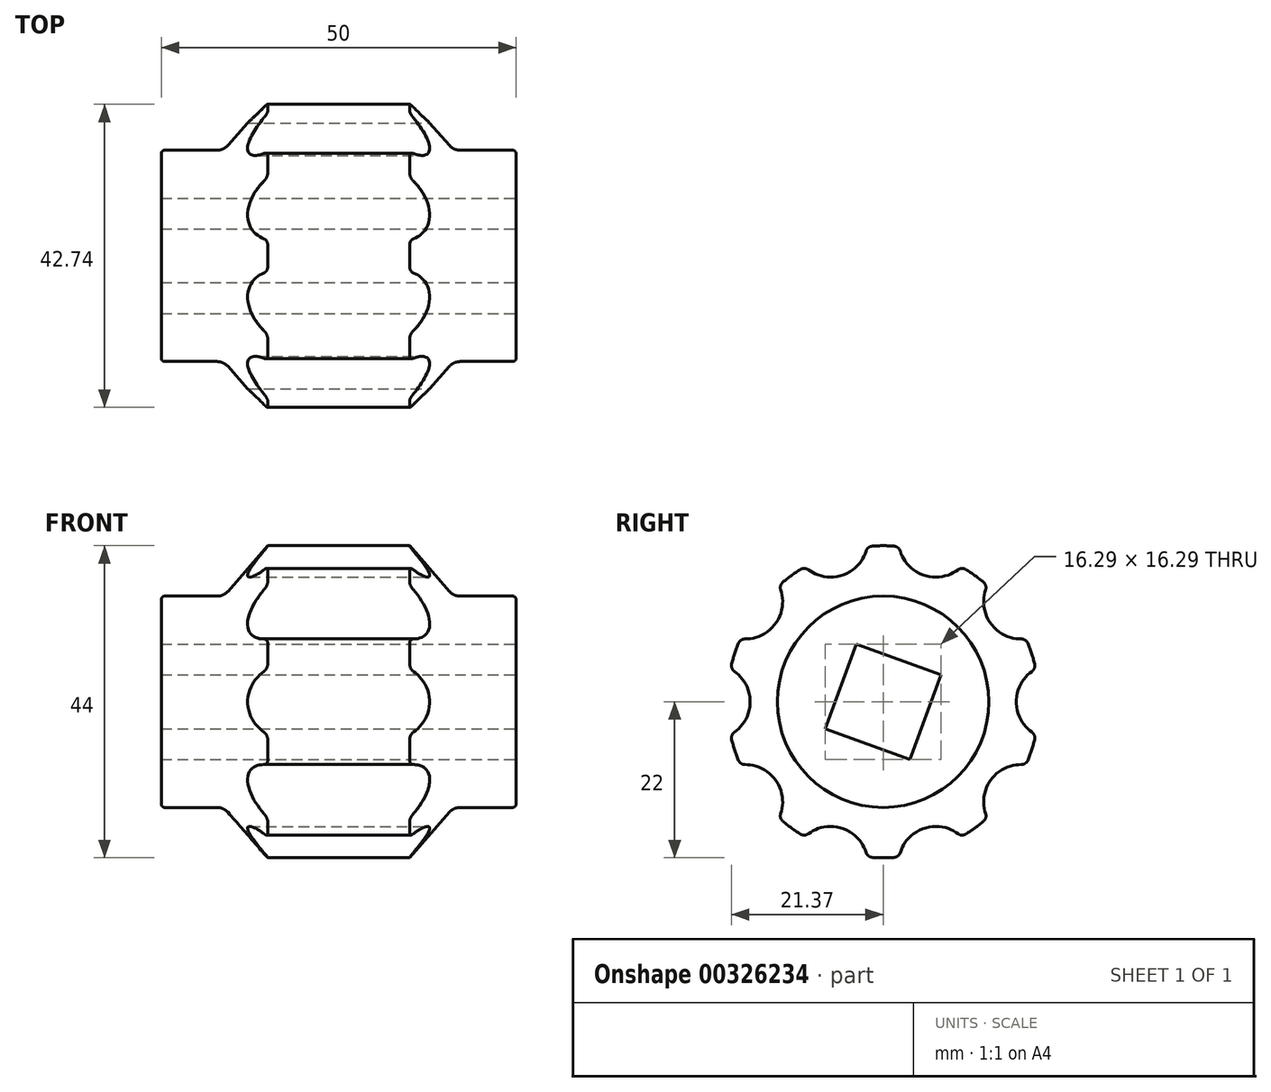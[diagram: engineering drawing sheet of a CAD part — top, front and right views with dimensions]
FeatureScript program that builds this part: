
annotation { "Feature Type Name" : "Feature", "Feature Type Description" : "" }
export const myFeature = defineFeature(function(context is Context, id is Id, definition is map)
    precondition{}
    {
        {
            var Q0;
            Q0=qCreatedBy(makeId("Front.planeOp"),FACE);
            var sketch = newSketch(context, id + "F0", { "sketchPlane" : qUnion([Q0])});
            skLineSegment(sketch, "E0", {"start": v(23, 5) * mm, "end": v(23, 14.9) * mm});
            skLineSegment(sketch, "E1", {"start": v(23, 14.9) * mm, "end": v(14.2, 14.9) * mm});
            skLineSegment(sketch, "E2", {"start": v(8, 22) * mm, "end": v(-12, 22) * mm});
            skLineSegment(sketch, "E3", {"start": v(-27, 14.9) * mm, "end": v(-27, 5) * mm});
            skLineSegment(sketch, "E4", {"start": v(-27, 5) * mm, "end": v(23, 5) * mm});
            skPoint(sketch, "E5.start.orphan", {"position": v(-27, 0) * mm});
            skLineSegment(sketch, "E6", {"start": v(-27, 0) * mm, "end": v(30.22, 0) * mm, "construction": true});
            skLineSegment(sketch, "E7", {"start": v(8, 22) * mm, "end": v(14.2, 14.9) * mm});
            skLineSegment(sketch, "E8", {"start": v(-27, 14.9) * mm, "end": v(-18.2, 14.9) * mm});
            skLineSegment(sketch, "E9", {"start": v(-18.2, 14.9) * mm, "end": v(-12, 22) * mm});
            skSolve(sketch);
        }
        {
            var Q0;
            Q0=makeQuery(id+"F0.imprint","IMPRINT",FACE,{"disambiguationData":[TD([[makeQuery(id+"F0.imprint","IMPRINT",EDGE,{"derivedFrom":sQuery(id+"F0.wireOp",EDGE,"E0")}),1.0]])]});
            var Q1;
            Q1=sQuery(id+"F0.wireOp",EDGE,"E6");
            revolve(context, id + "F1", {"entities" : qUnion([Q0]), "axis" : qUnion([Q1]), "revolveType" : RevolveType.FULL});
        }
        {
            var Q0;
            Q0=makeQuery(id+"F1.opRevolve","SWEPT_FACE",FACE,{"disambiguationData":[OSD([sQuery(id+"F0.wireOp",EDGE,"E0")])]});
            var sketch = newSketch(context, id + "F2", { "sketchPlane" : qUnion([Q0])});
            skCircle(sketch, "E10.cCircle", {"center": v(0, 0) * mm, "radius": 6.35 * mm, "construction": true});
            skLineSegment(sketch, "E10.0", {"start": v(8.14, 3.79) * mm, "end": v(3.79, -8.14) * mm});
            skLineSegment(sketch, "E10.1", {"start": v(3.79, -8.14) * mm, "end": v(-8.14, -3.79) * mm});
            skLineSegment(sketch, "E10.2", {"start": v(-8.14, -3.79) * mm, "end": v(-3.79, 8.14) * mm});
            skLineSegment(sketch, "E10.3", {"start": v(-3.79, 8.14) * mm, "end": v(8.14, 3.79) * mm});
            skPoint(sketch, "E10.0.midPoint", {"position": v(5.96, -2.18) * mm});
            skCircle(sketch, "E11", {"center": v(24, 0) * mm, "radius": 5.25 * mm});
            skCircle(sketch, "E12.1.0", {"center": v(19.42, 14.1) * mm, "radius": 5.25 * mm});
            skCircle(sketch, "E12.2.0", {"center": v(7.42, 22.83) * mm, "radius": 5.25 * mm});
            skCircle(sketch, "E12.3.0", {"center": v(-7.42, 22.83) * mm, "radius": 5.25 * mm});
            skCircle(sketch, "E12.4.0", {"center": v(-19.42, 14.1) * mm, "radius": 5.25 * mm});
            skCircle(sketch, "E12.5.0", {"center": v(-24, 0) * mm, "radius": 5.25 * mm});
            skCircle(sketch, "E12.6.0", {"center": v(-19.42, -14.1) * mm, "radius": 5.25 * mm});
            skCircle(sketch, "E12.7.0", {"center": v(-7.42, -22.83) * mm, "radius": 5.25 * mm});
            skCircle(sketch, "E12.8.0", {"center": v(7.42, -22.83) * mm, "radius": 5.25 * mm});
            skCircle(sketch, "E12.9.0", {"center": v(19.42, -14.1) * mm, "radius": 5.25 * mm});
            skSolve(sketch);
        }
        {
            var Q0;
            Q0=makeQuery(id+"F1.opRevolve","SWEPT_EDGE",EDGE,{"disambiguationData":[OSD([sQuery(id+"F0.wireOp",EDGE,"E3"),sQuery(id+"F0.wireOp",EDGE,"E8")])]});
            var Q1;
            Q1=makeQuery(id+"F1.opRevolve","SWEPT_EDGE",EDGE,{"disambiguationData":[OSD([sQuery(id+"F0.wireOp",EDGE,"E0"),sQuery(id+"F0.wireOp",EDGE,"E1")])]});
            fillet(context, id + "F3", {"entities" : qUnion([Q0, Q1]), "radius" : .5 * mm, "tangentPropagation" : true, "allowEdgeOverflow" : false});
        }
        {
            var Q0;
            Q0=makeQuery(id+"F2.imprint","IMPRINT",FACE,{"disambiguationData":[TD([[makeQuery(id+"F2.imprint","IMPRINT",EDGE,{"derivedFrom":sQuery(id+"F2.wireOp",EDGE,"E10.0")}),-1.0]])]});
            extrude(context, id + "F4", {"entities" : qUnion([Q0]), "operationType" : NewBodyOperationType.REMOVE, "oppositeDirection" : true, "depth" : 50 * mm, "offsetDistance" : 25 * mm});
        }
        {
            var Q0;
            Q0=makeQuery(id+"F2.imprint","IMPRINT",FACE,{"disambiguationData":[TD([[makeQuery(id+"F2.imprint","IMPRINT",EDGE,{"derivedFrom":sQuery(id+"F2.wireOp",EDGE,"E12.1.0")}),1.0]])]});
            var Q1;
            Q1=makeQuery(id+"F2.imprint","IMPRINT",FACE,{"disambiguationData":[TD([[makeQuery(id+"F2.imprint","IMPRINT",EDGE,{"derivedFrom":sQuery(id+"F2.wireOp",EDGE,"E11")}),1.0]])]});
            var Q2;
            Q2=makeQuery(id+"F2.imprint","IMPRINT",FACE,{"disambiguationData":[TD([[makeQuery(id+"F2.imprint","IMPRINT",EDGE,{"derivedFrom":sQuery(id+"F2.wireOp",EDGE,"E12.9.0")}),1.0]])]});
            var Q3;
            Q3=makeQuery(id+"F2.imprint","IMPRINT",FACE,{"disambiguationData":[TD([[makeQuery(id+"F2.imprint","IMPRINT",EDGE,{"derivedFrom":sQuery(id+"F2.wireOp",EDGE,"E12.8.0")}),1.0]])]});
            var Q4;
            Q4=makeQuery(id+"F2.imprint","IMPRINT",FACE,{"disambiguationData":[TD([[makeQuery(id+"F2.imprint","IMPRINT",EDGE,{"derivedFrom":sQuery(id+"F2.wireOp",EDGE,"E12.7.0")}),1.0]])]});
            var Q5;
            Q5=makeQuery(id+"F2.imprint","IMPRINT",FACE,{"disambiguationData":[TD([[makeQuery(id+"F2.imprint","IMPRINT",EDGE,{"derivedFrom":sQuery(id+"F2.wireOp",EDGE,"E12.6.0")}),1.0]])]});
            var Q6;
            Q6=makeQuery(id+"F2.imprint","IMPRINT",FACE,{"disambiguationData":[TD([[makeQuery(id+"F2.imprint","IMPRINT",EDGE,{"derivedFrom":sQuery(id+"F2.wireOp",EDGE,"E12.5.0")}),1.0]])]});
            var Q7;
            Q7=makeQuery(id+"F2.imprint","IMPRINT",FACE,{"disambiguationData":[TD([[makeQuery(id+"F2.imprint","IMPRINT",EDGE,{"derivedFrom":sQuery(id+"F2.wireOp",EDGE,"E12.3.0")}),1.0]])]});
            var Q8;
            Q8=makeQuery(id+"F2.imprint","IMPRINT",FACE,{"disambiguationData":[TD([[makeQuery(id+"F2.imprint","IMPRINT",EDGE,{"derivedFrom":sQuery(id+"F2.wireOp",EDGE,"E12.2.0")}),1.0]])]});
            var Q9;
            Q9=makeQuery(id+"F2.imprint","IMPRINT",FACE,{"disambiguationData":[TD([[makeQuery(id+"F2.imprint","IMPRINT",EDGE,{"derivedFrom":sQuery(id+"F2.wireOp",EDGE,"E12.4.0")}),1.0]])]});
            extrude(context, id + "F5", {"entities" : qUnion([Q0, Q1, Q2, Q3, Q4, Q5, Q6, Q7, Q8, Q9]), "operationType" : NewBodyOperationType.REMOVE, "oppositeDirection" : true, "depth" : 50 * mm});
        }
        {
            var Q0;
            Q0=makeQuery(id+"F1.opRevolve","SWEPT_EDGE",EDGE,{"disambiguationData":[OSD([sQuery(id+"F0.wireOp",EDGE,"E1"),sQuery(id+"F0.wireOp",EDGE,"lQtPVyIY-ggqZ-GcBV-1edM-0pXQkhYFdYdI")])]});
            var Q1;
            Q1=makeQuery(id+"F1.opRevolve","SWEPT_EDGE",EDGE,{"disambiguationData":[OSD([sQuery(id+"F0.wireOp",EDGE,"0TzLTUSK-P1le-NMfB-YZgS-nyDzrUtxSBo3"),sQuery(id+"F0.wireOp",EDGE,"mhRDrD4P-eXcN-jgfk-grpd-L3LYcjMJo5U6")])]});
            fillet(context, id + "F6", {"entities" : qUnion([Q0, Q1]), "radius" : 2 * mm, "tangentPropagation" : true, "allowEdgeOverflow" : false});
        }
        {
            var Q0;
            Q0=makeQuery(id+"F5.boolean.opBoolean","INTERSECT",EDGE,{"disambiguationData":[OD(1.0)],"derivedFrom":[makeQuery(id+"F1.opRevolve","SWEPT_FACE",FACE,{"disambiguationData":[OSD([sQuery(id+"F0.wireOp",EDGE,"E2")])]}),makeQuery(id+"F5.opExtrude","SWEPT_FACE",FACE,{"disambiguationData":[OSD([sQuery(id+"F2.wireOp",EDGE,"E12.2.0")])]})]});
            var Q1;
            Q1=makeQuery(id+"F5.boolean.opBoolean","INTERSECT",EDGE,{"disambiguationData":[OD(0.0)],"derivedFrom":[makeQuery(id+"F1.opRevolve","SWEPT_FACE",FACE,{"disambiguationData":[OSD([sQuery(id+"F0.wireOp",EDGE,"E2")])]}),makeQuery(id+"F5.opExtrude","SWEPT_FACE",FACE,{"disambiguationData":[OSD([sQuery(id+"F2.wireOp",EDGE,"E12.3.0")])]})]});
            var Q2;
            Q2=makeQuery(id+"F5.boolean.opBoolean","INTERSECT",EDGE,{"disambiguationData":[OD(0.0)],"derivedFrom":[makeQuery(id+"F1.opRevolve","SWEPT_FACE",FACE,{"disambiguationData":[OSD([sQuery(id+"F0.wireOp",EDGE,"E2")])]}),makeQuery(id+"F5.opExtrude","SWEPT_FACE",FACE,{"disambiguationData":[OSD([sQuery(id+"F2.wireOp",EDGE,"E12.2.0")])]})]});
            var Q3;
            Q3=makeQuery(id+"F5.boolean.opBoolean","INTERSECT",EDGE,{"disambiguationData":[OD(1.0)],"derivedFrom":[makeQuery(id+"F1.opRevolve","SWEPT_FACE",FACE,{"disambiguationData":[OSD([sQuery(id+"F0.wireOp",EDGE,"E2")])]}),makeQuery(id+"F5.opExtrude","SWEPT_FACE",FACE,{"disambiguationData":[OSD([sQuery(id+"F2.wireOp",EDGE,"E12.1.0")])]})]});
            var Q4;
            Q4=makeQuery(id+"F5.boolean.opBoolean","INTERSECT",EDGE,{"disambiguationData":[OD(0.0)],"derivedFrom":[makeQuery(id+"F1.opRevolve","SWEPT_FACE",FACE,{"disambiguationData":[OSD([sQuery(id+"F0.wireOp",EDGE,"E2")])]}),makeQuery(id+"F5.opExtrude","SWEPT_FACE",FACE,{"disambiguationData":[OSD([sQuery(id+"F2.wireOp",EDGE,"E12.1.0")])]})]});
            var Q5;
            Q5=makeQuery(id+"F5.boolean.opBoolean","INTERSECT",EDGE,{"disambiguationData":[OD(0.0)],"derivedFrom":[makeQuery(id+"F1.opRevolve","SWEPT_FACE",FACE,{"disambiguationData":[OSD([sQuery(id+"F0.wireOp",EDGE,"E2")])]}),makeQuery(id+"F5.opExtrude","SWEPT_FACE",FACE,{"disambiguationData":[OSD([sQuery(id+"F2.wireOp",EDGE,"E11")])]})]});
            var Q6;
            Q6=makeQuery(id+"F5.boolean.opBoolean","INTERSECT",EDGE,{"disambiguationData":[OD(1.0)],"derivedFrom":[makeQuery(id+"F1.opRevolve","SWEPT_FACE",FACE,{"disambiguationData":[OSD([sQuery(id+"F0.wireOp",EDGE,"E2")])]}),makeQuery(id+"F5.opExtrude","SWEPT_FACE",FACE,{"disambiguationData":[OSD([sQuery(id+"F2.wireOp",EDGE,"E11")])]})]});
            var Q7;
            Q7=makeQuery(id+"F5.boolean.opBoolean","INTERSECT",EDGE,{"disambiguationData":[OD(0.0)],"derivedFrom":[makeQuery(id+"F1.opRevolve","SWEPT_FACE",FACE,{"disambiguationData":[OSD([sQuery(id+"F0.wireOp",EDGE,"E2")])]}),makeQuery(id+"F5.opExtrude","SWEPT_FACE",FACE,{"disambiguationData":[OSD([sQuery(id+"F2.wireOp",EDGE,"E12.9.0")])]})]});
            var Q8;
            Q8=makeQuery(id+"F5.boolean.opBoolean","INTERSECT",EDGE,{"disambiguationData":[OD(1.0)],"derivedFrom":[makeQuery(id+"F1.opRevolve","SWEPT_FACE",FACE,{"disambiguationData":[OSD([sQuery(id+"F0.wireOp",EDGE,"E2")])]}),makeQuery(id+"F5.opExtrude","SWEPT_FACE",FACE,{"disambiguationData":[OSD([sQuery(id+"F2.wireOp",EDGE,"E12.9.0")])]})]});
            var Q9;
            Q9=makeQuery(id+"F5.boolean.opBoolean","INTERSECT",EDGE,{"disambiguationData":[OD(1.0)],"derivedFrom":[makeQuery(id+"F1.opRevolve","SWEPT_FACE",FACE,{"disambiguationData":[OSD([sQuery(id+"F0.wireOp",EDGE,"E2")])]}),makeQuery(id+"F5.opExtrude","SWEPT_FACE",FACE,{"disambiguationData":[OSD([sQuery(id+"F2.wireOp",EDGE,"E12.8.0")])]})]});
            var Q10;
            Q10=makeQuery(id+"F5.boolean.opBoolean","INTERSECT",EDGE,{"disambiguationData":[OD(0.0)],"derivedFrom":[makeQuery(id+"F1.opRevolve","SWEPT_FACE",FACE,{"disambiguationData":[OSD([sQuery(id+"F0.wireOp",EDGE,"E2")])]}),makeQuery(id+"F5.opExtrude","SWEPT_FACE",FACE,{"disambiguationData":[OSD([sQuery(id+"F2.wireOp",EDGE,"E12.8.0")])]})]});
            var Q11;
            Q11=makeQuery(id+"F5.boolean.opBoolean","INTERSECT",EDGE,{"disambiguationData":[OD(1.0)],"derivedFrom":[makeQuery(id+"F1.opRevolve","SWEPT_FACE",FACE,{"disambiguationData":[OSD([sQuery(id+"F0.wireOp",EDGE,"E2")])]}),makeQuery(id+"F5.opExtrude","SWEPT_FACE",FACE,{"disambiguationData":[OSD([sQuery(id+"F2.wireOp",EDGE,"E12.7.0")])]})]});
            var Q12;
            Q12=makeQuery(id+"F5.boolean.opBoolean","INTERSECT",EDGE,{"disambiguationData":[OD(0.0)],"derivedFrom":[makeQuery(id+"F1.opRevolve","SWEPT_FACE",FACE,{"disambiguationData":[OSD([sQuery(id+"F0.wireOp",EDGE,"E2")])]}),makeQuery(id+"F5.opExtrude","SWEPT_FACE",FACE,{"disambiguationData":[OSD([sQuery(id+"F2.wireOp",EDGE,"E12.7.0")])]})]});
            var Q13;
            Q13=makeQuery(id+"F5.boolean.opBoolean","INTERSECT",EDGE,{"disambiguationData":[OD(1.0)],"derivedFrom":[makeQuery(id+"F1.opRevolve","SWEPT_FACE",FACE,{"disambiguationData":[OSD([sQuery(id+"F0.wireOp",EDGE,"E2")])]}),makeQuery(id+"F5.opExtrude","SWEPT_FACE",FACE,{"disambiguationData":[OSD([sQuery(id+"F2.wireOp",EDGE,"E12.6.0")])]})]});
            var Q14;
            Q14=makeQuery(id+"F5.boolean.opBoolean","INTERSECT",EDGE,{"disambiguationData":[OD(0.0)],"derivedFrom":[makeQuery(id+"F1.opRevolve","SWEPT_FACE",FACE,{"disambiguationData":[OSD([sQuery(id+"F0.wireOp",EDGE,"E2")])]}),makeQuery(id+"F5.opExtrude","SWEPT_FACE",FACE,{"disambiguationData":[OSD([sQuery(id+"F2.wireOp",EDGE,"E12.6.0")])]})]});
            var Q15;
            Q15=makeQuery(id+"F5.boolean.opBoolean","INTERSECT",EDGE,{"disambiguationData":[OD(1.0)],"derivedFrom":[makeQuery(id+"F1.opRevolve","SWEPT_FACE",FACE,{"disambiguationData":[OSD([sQuery(id+"F0.wireOp",EDGE,"E2")])]}),makeQuery(id+"F5.opExtrude","SWEPT_FACE",FACE,{"disambiguationData":[OSD([sQuery(id+"F2.wireOp",EDGE,"E12.5.0")])]})]});
            var Q16;
            Q16=makeQuery(id+"F5.boolean.opBoolean","INTERSECT",EDGE,{"disambiguationData":[OD(0.0)],"derivedFrom":[makeQuery(id+"F1.opRevolve","SWEPT_FACE",FACE,{"disambiguationData":[OSD([sQuery(id+"F0.wireOp",EDGE,"E2")])]}),makeQuery(id+"F5.opExtrude","SWEPT_FACE",FACE,{"disambiguationData":[OSD([sQuery(id+"F2.wireOp",EDGE,"E12.5.0")])]})]});
            var Q17;
            Q17=makeQuery(id+"F5.boolean.opBoolean","INTERSECT",EDGE,{"disambiguationData":[OD(1.0)],"derivedFrom":[makeQuery(id+"F1.opRevolve","SWEPT_FACE",FACE,{"disambiguationData":[OSD([sQuery(id+"F0.wireOp",EDGE,"E2")])]}),makeQuery(id+"F5.opExtrude","SWEPT_FACE",FACE,{"disambiguationData":[OSD([sQuery(id+"F2.wireOp",EDGE,"E12.4.0")])]})]});
            var Q18;
            Q18=makeQuery(id+"F5.boolean.opBoolean","INTERSECT",EDGE,{"disambiguationData":[OD(0.0)],"derivedFrom":[makeQuery(id+"F1.opRevolve","SWEPT_FACE",FACE,{"disambiguationData":[OSD([sQuery(id+"F0.wireOp",EDGE,"E2")])]}),makeQuery(id+"F5.opExtrude","SWEPT_FACE",FACE,{"disambiguationData":[OSD([sQuery(id+"F2.wireOp",EDGE,"E12.4.0")])]})]});
            var Q19;
            Q19=makeQuery(id+"F5.boolean.opBoolean","INTERSECT",EDGE,{"disambiguationData":[OD(1.0)],"derivedFrom":[makeQuery(id+"F1.opRevolve","SWEPT_FACE",FACE,{"disambiguationData":[OSD([sQuery(id+"F0.wireOp",EDGE,"E2")])]}),makeQuery(id+"F5.opExtrude","SWEPT_FACE",FACE,{"disambiguationData":[OSD([sQuery(id+"F2.wireOp",EDGE,"E12.3.0")])]})]});
            fillet(context, id + "F7", {"entities" : qUnion([Q0, Q1, Q2, Q3, Q4, Q5, Q6, Q7, Q8, Q9, Q10, Q11, Q12, Q13, Q14, Q15, Q16, Q17, Q18, Q19]), "radius" : 1 * mm, "tangentPropagation" : true, "allowEdgeOverflow" : false});
        }
        {
            var Q0;
            Q0=makeQuery(id+"F1.opRevolve","SWEPT_EDGE",EDGE,{"disambiguationData":[OSD([sQuery(id+"F0.wireOp",EDGE,"E8"),sQuery(id+"F0.wireOp",EDGE,"E9")])]});
            fillet(context, id + "F8", {"entities" : qUnion([Q0]), "radius" : 2 * mm, "tangentPropagation" : true, "allowEdgeOverflow" : false});
        }
        {
            var Q0;
            Q0=makeQuery(id+"F1.opRevolve","SWEPT_BODY",BODY,{"disambiguationData":[OSD([sQuery(id+"F0.wireOp",EDGE,"E0"),sQuery(id+"F0.wireOp",EDGE,"E1"),sQuery(id+"F0.wireOp",EDGE,"E2"),sQuery(id+"F0.wireOp",EDGE,"E3"),sQuery(id+"F0.wireOp",EDGE,"E4"),sQuery(id+"F0.wireOp",EDGE,"E7"),sQuery(id+"F0.wireOp",EDGE,"E8"),sQuery(id+"F0.wireOp",EDGE,"E9")])]});
            transform(context, id + "F9", {"entities" : qUnion([Q0]), "transformType" : TransformType.TRANSLATION_3D, "dx" : 0 * mm, "dy" : 71.6 * mm, "dz" : 0 * mm, "makeCopy" : true});
        }
        {
            var Q0;
            Q0=makeQuery(id+"F9.opPattern","COPY",BODY,{"derivedFrom":makeQuery(id+"F1.opRevolve","SWEPT_BODY",BODY,{"disambiguationData":[OSD([sQuery(id+"F0.wireOp",EDGE,"E0"),sQuery(id+"F0.wireOp",EDGE,"E1"),sQuery(id+"F0.wireOp",EDGE,"E2"),sQuery(id+"F0.wireOp",EDGE,"E3"),sQuery(id+"F0.wireOp",EDGE,"E4"),sQuery(id+"F0.wireOp",EDGE,"E7"),sQuery(id+"F0.wireOp",EDGE,"E8"),sQuery(id+"F0.wireOp",EDGE,"E9")])]}),"instanceName":"1"});
            deleteBodies(context, id + "F10", {"entities" : qUnion([Q0])});
        }
    });
